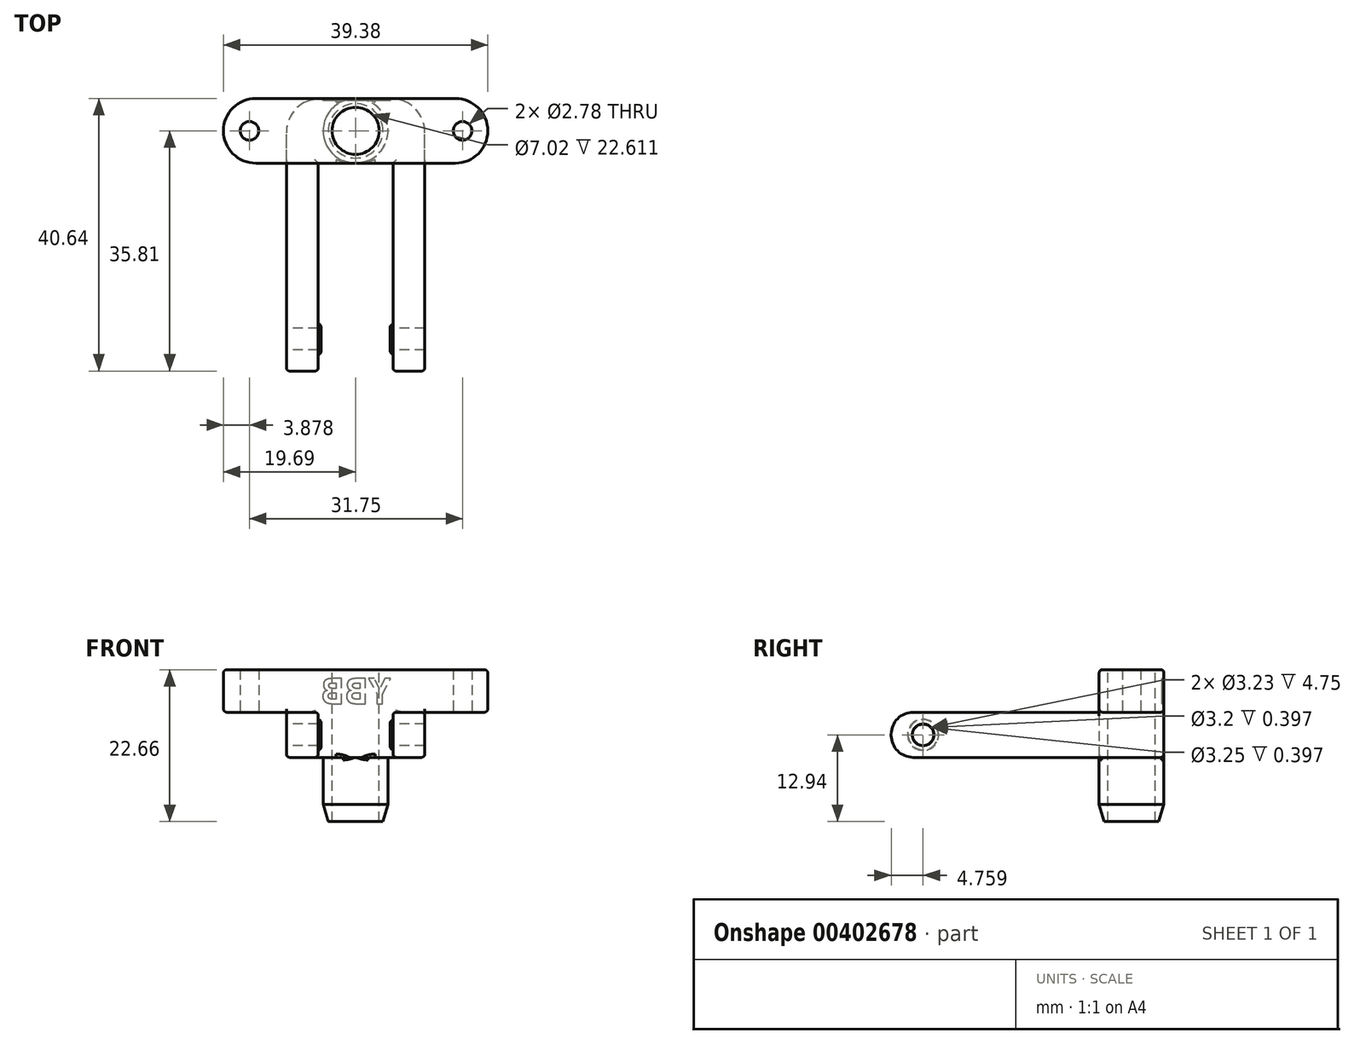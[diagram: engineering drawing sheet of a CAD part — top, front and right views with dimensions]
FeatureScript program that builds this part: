
annotation { "Feature Type Name" : "Feature", "Feature Type Description" : "" }
export const myFeature = defineFeature(function(context is Context, id is Id, definition is map)
    precondition{}
    {
        {
            var Q0;
            Q0=qCreatedBy(makeId("Top.planeOp"),FACE);
            var sketch = newSketch(context, id + "F0", { "sketchPlane" : qUnion([Q0])});
            skLineSegment(sketch, "E0.bottom", {"start": v(10.31, -4.83) * mm, "end": v(-10.31, -4.83) * mm});
            skLineSegment(sketch, "E0.top", {"start": v(10.31, 4.83) * mm, "end": v(-10.31, 4.83) * mm});
            skLineSegment(sketch, "E0.left", {"start": v(10.31, -4.83) * mm, "end": v(10.31, 4.83) * mm});
            skLineSegment(sketch, "E0.right", {"start": v(-10.31, -4.83) * mm, "end": v(-10.31, 4.83) * mm});
            skPoint(sketch, "E0.middle", {"position": v(0, 0) * mm});
            skCircle(sketch, "E1", {"center": v(0, 0) * mm, "radius": 3.2 * mm});
            skLineSegment(sketch, "E2.bottom", {"start": v(10.31, -4.83) * mm, "end": v(5.56, -4.83) * mm});
            skLineSegment(sketch, "E2.top", {"start": v(10.31, -35.81) * mm, "end": v(5.56, -35.81) * mm});
            skLineSegment(sketch, "E2.left", {"start": v(10.31, -4.83) * mm, "end": v(10.31, -35.81) * mm});
            skLineSegment(sketch, "E2.right", {"start": v(5.56, -4.83) * mm, "end": v(5.56, -35.81) * mm});
            skLineSegment(sketch, "E3.MirrorCS", {"start": v(-5.56, -4.83) * mm, "end": v(-5.56, -35.81) * mm});
            skLineSegment(sketch, "E4.MirrorCS", {"start": v(-10.31, -35.81) * mm, "end": v(-5.56, -35.81) * mm});
            skLineSegment(sketch, "E5.MirrorCS", {"start": v(-10.31, -4.83) * mm, "end": v(-10.31, -35.81) * mm});
            skSolve(sketch);
        }
        {
            var Q0;
            {var subQ8=sQuery(id+"F0.wireOp",EDGE,"E3.MirrorCS");Q0=qUnion([makeQuery(id+"F0.imprint","IMPRINT",FACE,{"disambiguationData":[TD([[makeQuery(id+"F0.imprint","IMPRINT",EDGE,{"derivedFrom":sQuery(id+"F0.wireOp",EDGE,"E0.top")}),1.0]])]}),makeQuery(id+"F0.imprint","IMPRINT",FACE,{"disambiguationData":[TD([[makeQuery(id+"F0.imprint","IMPRINT",EDGE,{"derivedFrom":subQ8}),-1.0]])]}),makeQuery(id+"F0.imprint","IMPRINT",FACE,{"disambiguationData":[TD([[makeQuery(id+"F0.imprint","IMPRINT",EDGE,{"derivedFrom":sQuery(id+"F0.wireOp",EDGE,"E2.top")}),-1.0]])]})]);}
            extrude(context, id + "F1", {"entities" : qUnion([Q0]), "endBound" : BoundingType.SYMMETRIC, "depth" : 6.73 * mm});
        }
        {
            var Q0;
            Q0=makeQuery(id+"F1.opExtrude","CAP_FACE",FACE,{"disambiguationData":[OSD([sQuery(id+"F0.wireOp",EDGE,"E0.bottom"),sQuery(id+"F0.wireOp",EDGE,"E0.top"),sQuery(id+"F0.wireOp",EDGE,"E0.left"),sQuery(id+"F0.wireOp",EDGE,"E0.right"),sQuery(id+"F0.wireOp",EDGE,"E1"),sQuery(id+"F0.wireOp",EDGE,"E2.top"),sQuery(id+"F0.wireOp",EDGE,"E2.left"),sQuery(id+"F0.wireOp",EDGE,"E2.right"),sQuery(id+"F0.wireOp",EDGE,"E3.MirrorCS"),sQuery(id+"F0.wireOp",EDGE,"E4.MirrorCS"),sQuery(id+"F0.wireOp",EDGE,"E5.MirrorCS")])],"isStart":true});
            var sketch = newSketch(context, id + "F2", { "sketchPlane" : qUnion([Q0])});
            skCircle(sketch, "E6", {"center": v(0, 0) * mm, "radius": 4.83 * mm});
            skCircle(sketch, "E7", {"center": v(0, 0) * mm, "radius": 3.15 * mm});
            skSolve(sketch);
        }
        {
            var Q0;
            Q0=makeQuery(id+"F1.opExtrude","SWEPT_FACE",FACE,{"disambiguationData":[OSD([sQuery(id+"F0.wireOp",EDGE,"E0.right"),sQuery(id+"F0.wireOp",EDGE,"E5.MirrorCS")])]});
            var sketch = newSketch(context, id + "F3", { "sketchPlane" : qUnion([Q0])});
            skCircle(sketch, "E8", {"center": v(31.05, 0) * mm, "radius": 1.61 * mm});
            skSolve(sketch);
        }
        {
            var Q0;
            Q0=qSketchRegion(id+"F3",true);
            extrude(context, id + "F4", {"entities" : qUnion([Q0]), "operationType" : NewBodyOperationType.REMOVE, "endBound" : BoundingType.THROUGH_ALL, "oppositeDirection" : true, "depth" : 25.4 * mm});
        }
        {
            var Q0;
            Q0=qSketchRegion(id+"F2",true);
            extrude(context, id + "F5", {"entities" : qUnion([Q0]), "operationType" : NewBodyOperationType.ADD, "depth" : 9.58 * mm});
        }
        {
            var Q0;
            Q0=makeQuery(id+"F1.opExtrude","SWEPT_FACE",FACE,{"disambiguationData":[OSD([sQuery(id+"F0.wireOp",EDGE,"E3.MirrorCS")])]});
            var sketch = newSketch(context, id + "F6", { "sketchPlane" : qUnion([Q0])});
            skCircle(sketch, "E9", {"center": v(-31.05, 0) * mm, "radius": 1.6 * mm});
            skCircle(sketch, "E10", {"center": v(-31.05, 0) * mm, "radius": 2.32 * mm});
            skSolve(sketch);
        }
        {
            var Q0;
            Q0=qSketchRegion(id+"F6",true);
            extrude(context, id + "F7", {"entities" : qUnion([Q0]), "operationType" : NewBodyOperationType.ADD, "depth" : 0.4 * mm, "offsetDistance" : 25.4 * mm});
        }
        {
            var Q0;
            Q0=makeQuery(id+"F1.opExtrude","SWEPT_FACE",FACE,{"disambiguationData":[OSD([sQuery(id+"F0.wireOp",EDGE,"E2.right")])]});
            var sketch = newSketch(context, id + "F8", { "sketchPlane" : qUnion([Q0])});
            skCircle(sketch, "E11", {"center": v(31.05, 0) * mm, "radius": 1.62 * mm});
            skCircle(sketch, "E12", {"center": v(31.05, 0) * mm, "radius": 2.25 * mm});
            skSolve(sketch);
        }
        {
            var Q0;
            Q0=qSketchRegion(id+"F8",true);
            extrude(context, id + "F9", {"entities" : qUnion([Q0]), "operationType" : NewBodyOperationType.ADD, "depth" : 0.4 * mm, "offsetDistance" : 25.4 * mm});
        }
        {
            var Q0;
            Q0=makeQuery(id+"F1.opExtrude","CAP_FACE",FACE,{"disambiguationData":[OSD([sQuery(id+"F0.wireOp",EDGE,"E0.bottom"),sQuery(id+"F0.wireOp",EDGE,"E0.top"),sQuery(id+"F0.wireOp",EDGE,"E0.left"),sQuery(id+"F0.wireOp",EDGE,"E0.right"),sQuery(id+"F0.wireOp",EDGE,"E1"),sQuery(id+"F0.wireOp",EDGE,"E2.top"),sQuery(id+"F0.wireOp",EDGE,"E2.left"),sQuery(id+"F0.wireOp",EDGE,"E2.right"),sQuery(id+"F0.wireOp",EDGE,"E3.MirrorCS"),sQuery(id+"F0.wireOp",EDGE,"E4.MirrorCS"),sQuery(id+"F0.wireOp",EDGE,"E5.MirrorCS")])],"isStart":false});
            var sketch = newSketch(context, id + "F10", { "sketchPlane" : qUnion([Q0])});
            skLineSegment(sketch, "E13.bottom", {"start": v(19.69, -4.83) * mm, "end": v(-19.69, -4.83) * mm});
            skLineSegment(sketch, "E13.top", {"start": v(19.68, 4.83) * mm, "end": v(-19.69, 4.83) * mm});
            skLineSegment(sketch, "E13.left", {"start": v(19.69, -4.83) * mm, "end": v(19.69, 4.83) * mm});
            skLineSegment(sketch, "E13.right", {"start": v(-19.69, -4.83) * mm, "end": v(-19.69, 4.83) * mm});
            skPoint(sketch, "E13.middle", {"position": v(0, 0) * mm});
            skCircle(sketch, "E14", {"center": v(0, 0) * mm, "radius": 3.21 * mm});
            skCircle(sketch, "E15", {"center": v(15.94, 0) * mm, "radius": 1.39 * mm});
            skCircle(sketch, "E16", {"center": v(-15.81, 0) * mm, "radius": 1.39 * mm});
            skSolve(sketch);
        }
        {
            var Q0;
            Q0=qSketchRegion(id+"F10",true);
            extrude(context, id + "F11", {"entities" : qUnion([Q0]), "operationType" : NewBodyOperationType.ADD, "depth" : 6.35 * mm});
        }
        {
            var Q0;
            Q0=makeQuery(id+"F11.opExtrude","CAP_EDGE",EDGE,{"disambiguationData":[OSD([sQuery(id+"F10.wireOp",EDGE,"E13.left")])],"isStart":false});
            var Q1;
            Q1=makeQuery(id+"F11.opExtrude","CAP_EDGE",EDGE,{"disambiguationData":[OSD([sQuery(id+"F10.wireOp",EDGE,"E13.top")])],"isStart":false});
            var Q2;
            Q2=makeQuery(id+"F11.opExtrude","CAP_EDGE",EDGE,{"disambiguationData":[OSD([sQuery(id+"F10.wireOp",EDGE,"E13.right")])],"isStart":false});
            var Q3;
            Q3=makeQuery(id+"F11.opExtrude","CAP_EDGE",EDGE,{"disambiguationData":[OSD([sQuery(id+"F10.wireOp",EDGE,"E13.bottom")])],"isStart":false});
            var Q4;
            Q4=makeQuery(id+"F11.opExtrude","CAP_EDGE",EDGE,{"disambiguationData":[OSD([sQuery(id+"F10.wireOp",EDGE,"E14")])],"isStart":false});
            var Q5;
            {var subQ2=sQuery(id+"F0.wireOp",EDGE,"E0.bottom");var subQ3=sQuery(id+"F10.wireOp",EDGE,"E13.bottom");var subQ4=makeQuery(id+"F11.opExtrude","SWEPT_FACE",FACE,{"disambiguationData":[OSD([subQ3])]});var subQ5=makeQuery(id+"F1.opExtrude","SWEPT_FACE",FACE,{"disambiguationData":[OSD([subQ2])]});var subQ6=sQuery(id+"F10.wireOp",EDGE,"E13.right");var subQ7=makeQuery(id+"F11.opExtrude","CAP_FACE",FACE,{"disambiguationData":[OSD([subQ3,sQuery(id+"F10.wireOp",EDGE,"E13.top"),sQuery(id+"F10.wireOp",EDGE,"E13.left"),subQ6,sQuery(id+"F10.wireOp",EDGE,"E14"),sQuery(id+"F10.wireOp",EDGE,"E15"),sQuery(id+"F10.wireOp",EDGE,"E16")])],"isStart":true});Q5=makeQuery(id+"F11.boolean.opBoolean","SPLIT",EDGE,{"disambiguationData":[topologyDisambiguationEdgeConnected([subQ5,subQ4,subQ7]),TD([makeQuery(id+"F11.opExtrude","SWEPT_FACE",FACE,{"disambiguationData":[OSD([subQ6])]})])],"derivedFrom":makeQuery(id+"F11.opExtrude","CAP_EDGE",EDGE,{"disambiguationData":[OSD([subQ3])],"isStart":true})});}
            var Q6;
            {var subQ2=sQuery(id+"F10.wireOp",EDGE,"E13.left");var subQ3=sQuery(id+"F10.wireOp",EDGE,"E13.bottom");var subQ4=makeQuery(id+"F11.opExtrude","CAP_FACE",FACE,{"disambiguationData":[OSD([subQ3,sQuery(id+"F10.wireOp",EDGE,"E13.top"),subQ2,sQuery(id+"F10.wireOp",EDGE,"E13.right"),sQuery(id+"F10.wireOp",EDGE,"E14"),sQuery(id+"F10.wireOp",EDGE,"E15"),sQuery(id+"F10.wireOp",EDGE,"E16")])],"isStart":true});var subQ5=sQuery(id+"F0.wireOp",EDGE,"E0.bottom");var subQ6=makeQuery(id+"F11.opExtrude","SWEPT_FACE",FACE,{"disambiguationData":[OSD([subQ3])]});var subQ7=makeQuery(id+"F1.opExtrude","SWEPT_FACE",FACE,{"disambiguationData":[OSD([subQ5])]});Q6=makeQuery(id+"F11.boolean.opBoolean","SPLIT",EDGE,{"disambiguationData":[topologyDisambiguationEdgeConnected([subQ7,subQ6,subQ4]),TD([makeQuery(id+"F11.opExtrude","SWEPT_FACE",FACE,{"disambiguationData":[OSD([subQ2])]})])],"derivedFrom":makeQuery(id+"F11.opExtrude","CAP_EDGE",EDGE,{"disambiguationData":[OSD([subQ3])],"isStart":true})});}
            var Q7;
            Q7=makeQuery(id+"F11.opExtrude","CAP_EDGE",EDGE,{"disambiguationData":[OSD([sQuery(id+"F10.wireOp",EDGE,"E13.left")])],"isStart":true});
            var Q8;
            {var subQ0=sQuery(id+"F10.wireOp",EDGE,"E13.top");var subQ1=sQuery(id+"F10.wireOp",EDGE,"E13.left");Q8=makeQuery(id+"F11.boolean.opBoolean","SPLIT",EDGE,{"disambiguationData":[TD([makeQuery(id+"F11.opExtrude","SWEPT_FACE",FACE,{"disambiguationData":[OSD([subQ1])]})])],"derivedFrom":makeQuery(id+"F11.opExtrude","CAP_EDGE",EDGE,{"disambiguationData":[OSD([subQ0])],"isStart":true})});}
            var Q9;
            {var subQ0=sQuery(id+"F10.wireOp",EDGE,"E13.top");var subQ1=sQuery(id+"F10.wireOp",EDGE,"E13.right");Q9=makeQuery(id+"F11.boolean.opBoolean","SPLIT",EDGE,{"disambiguationData":[TD([makeQuery(id+"F11.opExtrude","SWEPT_FACE",FACE,{"disambiguationData":[OSD([subQ1])]})])],"derivedFrom":makeQuery(id+"F11.opExtrude","CAP_EDGE",EDGE,{"disambiguationData":[OSD([subQ0])],"isStart":true})});}
            var Q10;
            Q10=makeQuery(id+"F11.opExtrude","CAP_EDGE",EDGE,{"disambiguationData":[OSD([sQuery(id+"F10.wireOp",EDGE,"E13.right")])],"isStart":true});
            fillet(context, id + "F12", {"entities" : qUnion([Q0, Q1, Q2, Q3, Q4, Q5, Q6, Q7, Q8, Q9, Q10]), "radius" : 0.5 * mm, "allowEdgeOverflow" : false});
        }
        {
            var Q0;
            Q0=makeQuery(id+"F1.opExtrude","CAP_EDGE",EDGE,{"disambiguationData":[OSD([sQuery(id+"F0.wireOp",EDGE,"E3.MirrorCS")])],"isStart":false});
            var Q1;
            Q1=makeQuery(id+"F7.opExtrude","CAP_EDGE",EDGE,{"disambiguationData":[OSD([sQuery(id+"F6.wireOp",EDGE,"E10")])],"isStart":false});
            var Q2;
            Q2=makeQuery(id+"F1.opExtrude","CAP_EDGE",EDGE,{"disambiguationData":[OSD([sQuery(id+"F0.wireOp",EDGE,"E2.right")])],"isStart":false});
            var Q3;
            Q3=makeQuery(id+"F9.opExtrude","CAP_EDGE",EDGE,{"disambiguationData":[OSD([sQuery(id+"F8.wireOp",EDGE,"E12")])],"isStart":false});
            fillet(context, id + "F13", {"entities" : qUnion([Q0, Q1, Q2, Q3]), "radius" : 0.5 * mm, "tangentPropagation" : true, "allowEdgeOverflow" : false});
        }
        {
            var Q0;
            Q0=makeQuery(id+"F5.boolean.opBoolean","SPLIT",EDGE,{"disambiguationData":[OD(0.0)],"derivedFrom":makeQuery(id+"F5.opExtrude","CAP_EDGE",EDGE,{"disambiguationData":[OSD([sQuery(id+"F2.wireOp",EDGE,"E6")])],"isStart":true})});
            var Q1;
            Q1=makeQuery(id+"F5.boolean.opBoolean","SPLIT",EDGE,{"disambiguationData":[OD(1.0)],"derivedFrom":makeQuery(id+"F5.opExtrude","CAP_EDGE",EDGE,{"disambiguationData":[OSD([sQuery(id+"F2.wireOp",EDGE,"E6")])],"isStart":true})});
            fillet(context, id + "F14", {"entities" : qUnion([Q0, Q1]), "radius" : 0.38 * mm, "tangentPropagation" : true, "allowEdgeOverflow" : false});
        }
        {
            var Q0;
            Q0=makeQuery(id+"F1.opExtrude","SWEPT_EDGE",EDGE,{"disambiguationData":[OSD([sQuery(id+"F0.wireOp",EDGE,"E3.MirrorCS"),sQuery(id+"F0.wireOp",EDGE,"E4.MirrorCS")])]});
            var Q1;
            Q1=makeQuery(id+"F1.opExtrude","SWEPT_EDGE",EDGE,{"disambiguationData":[OSD([sQuery(id+"F0.wireOp",EDGE,"E2.top"),sQuery(id+"F0.wireOp",EDGE,"E2.right")])]});
            var Q2;
            {var subQ0=sQuery(id+"F0.wireOp",EDGE,"E5.MirrorCS");var subQ1=sQuery(id+"F0.wireOp",EDGE,"E0.right");Q2=makeQuery(id+"F11.boolean.opBoolean","SPLIT",EDGE,{"disambiguationData":[topologyDisambiguationEdgeConnected([makeQuery(id+"F1.opExtrude","CAP_FACE",FACE,{"disambiguationData":[OSD([sQuery(id+"F0.wireOp",EDGE,"E0.bottom"),sQuery(id+"F0.wireOp",EDGE,"E0.top"),sQuery(id+"F0.wireOp",EDGE,"E0.left"),subQ1,sQuery(id+"F0.wireOp",EDGE,"E1"),sQuery(id+"F0.wireOp",EDGE,"E2.top"),sQuery(id+"F0.wireOp",EDGE,"E2.left"),sQuery(id+"F0.wireOp",EDGE,"E2.right"),sQuery(id+"F0.wireOp",EDGE,"E3.MirrorCS"),sQuery(id+"F0.wireOp",EDGE,"E4.MirrorCS"),subQ0])],"isStart":false})])],"derivedFrom":makeQuery(id+"F1.opExtrude","CAP_EDGE",EDGE,{"disambiguationData":[OSD([subQ1,subQ0])],"isStart":false})});}
            var Q3;
            Q3=makeQuery(id+"F1.opExtrude","SWEPT_EDGE",EDGE,{"disambiguationData":[OSD([sQuery(id+"F0.wireOp",EDGE,"E4.MirrorCS"),sQuery(id+"F0.wireOp",EDGE,"E5.MirrorCS")])]});
            var Q4;
            Q4=makeQuery(id+"F1.opExtrude","CAP_EDGE",EDGE,{"disambiguationData":[OSD([sQuery(id+"F0.wireOp",EDGE,"E0.right"),sQuery(id+"F0.wireOp",EDGE,"E5.MirrorCS")])],"isStart":true});
            var Q5;
            {var subQ0=sQuery(id+"F0.wireOp",EDGE,"E5.MirrorCS");var subQ1=sQuery(id+"F0.wireOp",EDGE,"E0.right");var subQ2=sQuery(id+"F0.wireOp",EDGE,"E0.top");Q5=makeQuery(id+"F5.boolean.opBoolean","SPLIT",EDGE,{"disambiguationData":[TD([makeQuery(id+"F1.opExtrude","SWEPT_FACE",FACE,{"disambiguationData":[OSD([subQ1,subQ0])]})])],"derivedFrom":makeQuery(id+"F1.opExtrude","CAP_EDGE",EDGE,{"disambiguationData":[OSD([subQ2])],"isStart":true})});}
            var Q6;
            {var subQ0=sQuery(id+"F0.wireOp",EDGE,"E2.left");var subQ1=sQuery(id+"F0.wireOp",EDGE,"E0.left");var subQ2=sQuery(id+"F0.wireOp",EDGE,"E0.top");Q6=makeQuery(id+"F5.boolean.opBoolean","SPLIT",EDGE,{"disambiguationData":[TD([makeQuery(id+"F1.opExtrude","SWEPT_FACE",FACE,{"disambiguationData":[OSD([subQ1,subQ0])]})])],"derivedFrom":makeQuery(id+"F1.opExtrude","CAP_EDGE",EDGE,{"disambiguationData":[OSD([subQ2])],"isStart":true})});}
            var Q7;
            {var subQ0=sQuery(id+"F0.wireOp",EDGE,"E0.bottom");var subQ1=sQuery(id+"F0.wireOp",EDGE,"E3.MirrorCS");Q7=makeQuery(id+"F5.boolean.opBoolean","SPLIT",EDGE,{"disambiguationData":[TD([makeQuery(id+"F1.opExtrude","SWEPT_FACE",FACE,{"disambiguationData":[OSD([subQ1])]})])],"derivedFrom":makeQuery(id+"F1.opExtrude","CAP_EDGE",EDGE,{"disambiguationData":[OSD([subQ0])],"isStart":true})});}
            var Q8;
            Q8=makeQuery(id+"F1.opExtrude","CAP_EDGE",EDGE,{"disambiguationData":[OSD([sQuery(id+"F0.wireOp",EDGE,"E3.MirrorCS")])],"isStart":true});
            var Q9;
            {var subQ0=sQuery(id+"F0.wireOp",EDGE,"E0.bottom");var subQ1=sQuery(id+"F0.wireOp",EDGE,"E2.right");Q9=makeQuery(id+"F5.boolean.opBoolean","SPLIT",EDGE,{"disambiguationData":[TD([makeQuery(id+"F1.opExtrude","SWEPT_FACE",FACE,{"disambiguationData":[OSD([subQ1])]})])],"derivedFrom":makeQuery(id+"F1.opExtrude","CAP_EDGE",EDGE,{"disambiguationData":[OSD([subQ0])],"isStart":true})});}
            var Q10;
            Q10=makeQuery(id+"F1.opExtrude","CAP_EDGE",EDGE,{"disambiguationData":[OSD([sQuery(id+"F0.wireOp",EDGE,"E2.right")])],"isStart":true});
            var Q11;
            Q11=makeQuery(id+"F1.opExtrude","CAP_EDGE",EDGE,{"disambiguationData":[OSD([sQuery(id+"F0.wireOp",EDGE,"E0.left"),sQuery(id+"F0.wireOp",EDGE,"E2.left")])],"isStart":true});
            var Q12;
            Q12=makeQuery(id+"F1.opExtrude","SWEPT_EDGE",EDGE,{"disambiguationData":[OSD([sQuery(id+"F0.wireOp",EDGE,"E2.top"),sQuery(id+"F0.wireOp",EDGE,"E2.left")])]});
            var Q13;
            {var subQ0=sQuery(id+"F0.wireOp",EDGE,"E2.left");var subQ1=sQuery(id+"F0.wireOp",EDGE,"E0.left");Q13=makeQuery(id+"F11.boolean.opBoolean","SPLIT",EDGE,{"disambiguationData":[topologyDisambiguationEdgeConnected([makeQuery(id+"F1.opExtrude","CAP_FACE",FACE,{"disambiguationData":[OSD([sQuery(id+"F0.wireOp",EDGE,"E0.bottom"),sQuery(id+"F0.wireOp",EDGE,"E0.top"),subQ1,sQuery(id+"F0.wireOp",EDGE,"E0.right"),sQuery(id+"F0.wireOp",EDGE,"E1"),sQuery(id+"F0.wireOp",EDGE,"E2.top"),subQ0,sQuery(id+"F0.wireOp",EDGE,"E2.right"),sQuery(id+"F0.wireOp",EDGE,"E3.MirrorCS"),sQuery(id+"F0.wireOp",EDGE,"E4.MirrorCS"),sQuery(id+"F0.wireOp",EDGE,"E5.MirrorCS")])],"isStart":false})])],"derivedFrom":makeQuery(id+"F1.opExtrude","CAP_EDGE",EDGE,{"disambiguationData":[OSD([subQ1,subQ0])],"isStart":false})});}
            fillet(context, id + "F15", {"entities" : qUnion([Q0, Q1, Q2, Q3, Q4, Q5, Q6, Q7, Q8, Q9, Q10, Q11, Q12, Q13]), "radius" : 0.5 * mm, "allowEdgeOverflow" : false});
        }
        {
            var Q0;
            Q0=makeQuery(id+"F1.opExtrude","CAP_EDGE",EDGE,{"disambiguationData":[OSD([sQuery(id+"F0.wireOp",EDGE,"E4.MirrorCS")])],"isStart":true});
            var Q1;
            Q1=makeQuery(id+"F1.opExtrude","CAP_EDGE",EDGE,{"disambiguationData":[OSD([sQuery(id+"F0.wireOp",EDGE,"E2.top")])],"isStart":true});
            var Q2;
            Q2=makeQuery(id+"F1.opExtrude","CAP_EDGE",EDGE,{"disambiguationData":[OSD([sQuery(id+"F0.wireOp",EDGE,"E2.top")])],"isStart":false});
            var Q3;
            Q3=makeQuery(id+"F1.opExtrude","CAP_EDGE",EDGE,{"disambiguationData":[OSD([sQuery(id+"F0.wireOp",EDGE,"E4.MirrorCS")])],"isStart":false});
            fillet(context, id + "F16", {"entities" : qUnion([Q0, Q1, Q2, Q3]), "radius" : 3.3 * mm, "tangentPropagation" : true, "allowEdgeOverflow" : false});
        }
        {
            var Q0;
            Q0=makeQuery(id+"F11.opExtrude","SWEPT_EDGE",EDGE,{"disambiguationData":[OSD([sQuery(id+"F10.wireOp",EDGE,"E13.bottom"),sQuery(id+"F10.wireOp",EDGE,"E13.right")])]});
            var Q1;
            Q1=makeQuery(id+"F11.opExtrude","SWEPT_EDGE",EDGE,{"disambiguationData":[OSD([sQuery(id+"F10.wireOp",EDGE,"E13.top"),sQuery(id+"F10.wireOp",EDGE,"E13.right")])]});
            var Q2;
            Q2=makeQuery(id+"F11.opExtrude","SWEPT_EDGE",EDGE,{"disambiguationData":[OSD([sQuery(id+"F10.wireOp",EDGE,"E13.top"),sQuery(id+"F10.wireOp",EDGE,"E13.left")])]});
            var Q3;
            Q3=makeQuery(id+"F11.opExtrude","SWEPT_EDGE",EDGE,{"disambiguationData":[OSD([sQuery(id+"F10.wireOp",EDGE,"E13.bottom"),sQuery(id+"F10.wireOp",EDGE,"E13.left")])]});
            fillet(context, id + "F17", {"entities" : qUnion([Q0, Q1, Q2, Q3]), "radius" : 4.83 * mm, "tangentPropagation" : true, "allowEdgeOverflow" : false});
        }
        {
            var Q0;
            Q0=makeQuery(id+"F1.opExtrude","SWEPT_EDGE",EDGE,{"disambiguationData":[OSD([sQuery(id+"F0.wireOp",EDGE,"E0.top"),sQuery(id+"F0.wireOp",EDGE,"E0.left")])]});
            var Q1;
            Q1=makeQuery(id+"F1.opExtrude","SWEPT_EDGE",EDGE,{"disambiguationData":[OSD([sQuery(id+"F0.wireOp",EDGE,"E0.top"),sQuery(id+"F0.wireOp",EDGE,"E0.right")])]});
            fillet(context, id + "F18", {"entities" : qUnion([Q0, Q1]), "radius" : 5.08 * mm, "tangentPropagation" : true, "allowEdgeOverflow" : false});
        }
        {
            var Q0;
            Q0=makeQuery(id+"F5.opExtrude","CAP_EDGE",EDGE,{"disambiguationData":[OSD([sQuery(id+"F2.wireOp",EDGE,"E6")])],"isStart":false});
            chamfer(context, id + "F19", {"entities" : qUnion([Q0]), "chamferType" : ChamferType.TWO_OFFSETS, "width1" : 0.76 * mm, "oppositeDirection" : false, "width2" : 2.54 * mm, "tangentPropagation" : true});
        }
        {
            var Q0;
            Q0=makeQuery(id+"F11.opExtrude","CAP_FACE",FACE,{"disambiguationData":[OSD([sQuery(id+"F10.wireOp",EDGE,"E13.bottom"),sQuery(id+"F10.wireOp",EDGE,"E13.top"),sQuery(id+"F10.wireOp",EDGE,"E13.left"),sQuery(id+"F10.wireOp",EDGE,"E13.right"),sQuery(id+"F10.wireOp",EDGE,"E14"),sQuery(id+"F10.wireOp",EDGE,"E15"),sQuery(id+"F10.wireOp",EDGE,"5532dd9e-91bd-412b-a6f8-db201805de330.MirrorC")])],"isStart":false});
            var sketch = newSketch(context, id + "F20", { "sketchPlane" : qUnion([Q0])});
            skCircle(sketch, "E17", {"center": v(0, 0) * mm, "radius": 3.5 * mm});
            skSolve(sketch);
        }
        {
            var Q0;
            Q0=qSketchRegion(id+"F20",true);
            extrude(context, id + "F21", {"entities" : qUnion([Q0]), "operationType" : NewBodyOperationType.REMOVE, "oppositeDirection" : true, "depth" : 38.1 * mm});
        }
        {
            var Q0;
            Q0=makeQuery(id+"F11.boolean.opBoolean","MERGE",FACE,{"derivedFrom":[makeQuery(id+"F1.opExtrude","SWEPT_FACE",FACE,{"disambiguationData":[OSD([sQuery(id+"F0.wireOp",EDGE,"E0.top")])]}),makeQuery(id+"F11.opExtrude","SWEPT_FACE",FACE,{"disambiguationData":[OSD([sQuery(id+"F10.wireOp",EDGE,"E13.top")])]})]});
            var sketch = newSketch(context, id + "F22", { "sketchPlane" : qUnion([Q0])});
            skText(sketch, "E18", { "text": "YBB", "fontName": "OpenSans-Bold.ttf"});
            const initialGuessF22  = {"E18": [-0.00522, 0.00464, 1, 0, 0.0038]};
            skSetInitialGuess(sketch, initialGuessF22);
            skSolve(sketch);
        }
        {
            var Q0;
            Q0=qSketchRegion(id+"F22",true);
            extrude(context, id + "F23", {"entities" : qUnion([Q0]), "operationType" : NewBodyOperationType.REMOVE, "oppositeDirection" : true, "depth" : 0.25 * mm, "offsetDistance" : 25.4 * mm});
        }
    });
